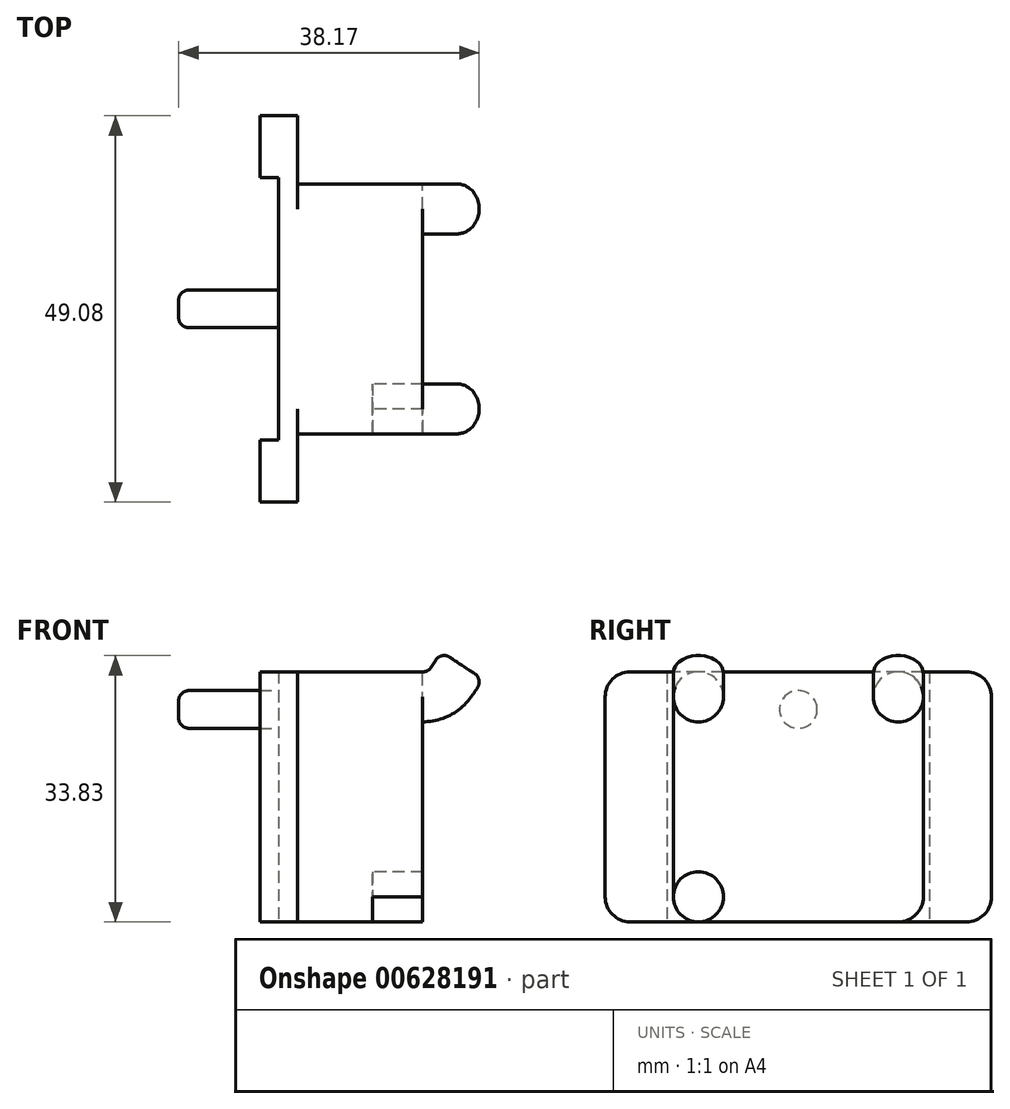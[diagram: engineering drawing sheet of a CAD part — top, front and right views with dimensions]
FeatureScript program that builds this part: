
annotation { "Feature Type Name" : "Feature", "Feature Type Description" : "" }
export const myFeature = defineFeature(function(context is Context, id is Id, definition is map)
    precondition{}
    {
        {
            var Q0;
            Q0=qCreatedBy(makeId("Right.planeOp"),FACE);
            var sketch = newSketch(context, id + "F0", { "sketchPlane" : qUnion([Q0])});
            skLineSegment(sketch, "E0.bottom", {"start": v(15.88, -15.87) * mm, "end": v(-15.88, -15.88) * mm});
            skLineSegment(sketch, "E0.top", {"start": v(15.88, 15.88) * mm, "end": v(-15.88, 15.88) * mm});
            skLineSegment(sketch, "E0.left", {"start": v(15.88, -15.87) * mm, "end": v(15.88, 15.88) * mm});
            skLineSegment(sketch, "E0.right", {"start": v(-15.88, -15.88) * mm, "end": v(-15.88, 15.88) * mm});
            skPoint(sketch, "E0.middle", {"position": v(0, 0) * mm});
            skSolve(sketch);
        }
        {
            var Q0;
            Q0=makeQuery(id+"F0.imprint","IMPRINT",FACE,{"disambiguationData":[TD([[makeQuery(id+"F0.imprint","IMPRINT",EDGE,{"derivedFrom":sQuery(id+"F0.wireOp",EDGE,"E0.bottom")}),-1.0]])]});
            extrude(context, id + "F1", {"entities" : qUnion([Q0]), "depth" : 9.52 * mm, "offsetDistance" : 25.4 * mm});
        }
        {
            var Q0;
            Q0=makeQuery(id+"F1.opExtrude","CAP_FACE",FACE,{"disambiguationData":[OSD([sQuery(id+"F0.wireOp",EDGE,"E0.bottom"),sQuery(id+"F0.wireOp",EDGE,"E0.top"),sQuery(id+"F0.wireOp",EDGE,"E0.left"),sQuery(id+"F0.wireOp",EDGE,"E0.right")])],"isStart":false});
            var sketch = newSketch(context, id + "F2", { "sketchPlane" : qUnion([Q0])});
            skCircle(sketch, "E1", {"center": v(-12.7, 12.7) * mm, "radius": 3.18 * mm});
            skLineSegment(sketch, "E2", {"start": v(-24.57, 0) * mm, "end": v(19.39, 0) * mm, "construction": true});
            skPoint(sketch, "E2.endSnap0", {"position": v(-15.88, 0) * mm});
            skLineSegment(sketch, "E3", {"start": v(0, 20.38) * mm, "end": v(0, -18.88) * mm, "construction": true});
            skCircle(sketch, "E4.MirrorC", {"center": v(-12.7, -12.7) * mm, "radius": 3.18 * mm});
            skLineSegment(sketch, "E5.MirrorCS", {"start": v(0, -20.38) * mm, "end": v(0, 18.88) * mm, "construction": true});
            skCircle(sketch, "E6.MirrorC", {"center": v(12.7, 12.7) * mm, "radius": 3.18 * mm});
            skCircle(sketch, "E7.MirrorC", {"center": v(12.7, -12.7) * mm, "radius": 3.18 * mm});
            skLineSegment(sketch, "E8", {"start": v(-12.7, 15.88) * mm, "end": v(-12.7, -15.88) * mm, "construction": true});
            skLineSegment(sketch, "E9", {"start": v(-15.88, 12.7) * mm, "end": v(15.88, 12.7) * mm, "construction": true});
            skPoint(sketch, "E10", {"position": v(-12.7, 15.88) * mm});
            skPoint(sketch, "E11", {"position": v(0, 0) * mm});
            skSolve(sketch);
        }
        {
            var Q0;
            Q0=makeQuery(id+"F1.opExtrude","SWEPT_FACE",FACE,{"disambiguationData":[OSD([sQuery(id+"F0.wireOp",EDGE,"E0.top")])]});
            var sketch = newSketch(context, id + "F3", { "sketchPlane" : qUnion([Q0])});
            skLineSegment(sketch, "E12", {"start": v(0, -12.7) * mm, "end": v(9.53, -12.7) * mm, "construction": true});
            skSolve(sketch);
        }
        {
            var Q0;
            Q0=sQuery(id+"F3.wireOp",VERTEX,"E12.start");
            var Q1;
            Q1=sQuery(id+"F2.wireOp",VERTEX,"E10");
            var Q2;
            Q2=sQuery(id+"F2.wireOp",VERTEX,"E8.end");
            cPlane(context, id + "F4", {"entities" : qUnion([Q0, Q1, Q2]), "cplaneType" : CPlaneType.THREE_POINT, "offset" : 25.4 * mm, "width" : 152.4 * mm, "height" : 152.4 * mm});
        }
        {
            var Q0;
            Q0=qCreatedBy(id+"F4.planeOp",FACE);
            var sketch = newSketch(context, id + "F5", { "sketchPlane" : qUnion([Q0])});
            skLineSegment(sketch, "E13", {"start": v(9.53, 9.53) * mm, "end": v(9.53, 15.88) * mm});
            skLineSegment(sketch, "E14", {"start": v(9.53, 9.53) * mm, "end": v(15.88, 9.53) * mm});
            skArc(sketch, "E15", {"start": v(15.88, 9.53) * mm, "mid": v(19.48, 10.43) * mm, "end": v(22.23, 12.93) * mm});
            skLineSegment(sketch, "E16", {"start": v(22.23, 12.93) * mm, "end": v(23.55, 14.93) * mm});
            skSolve(sketch);
        }
        {
            var Q0;
            {var subQ0=sQuery(id+"F2.wireOp",EDGE,"E1");var subQ1=makeQuery(id+"F2.imprint","INTERSECT",VERTEX,{"derivedFrom":[makeQuery(id+"F1.opExtrude","CAP_EDGE",EDGE,{"disambiguationData":[OSD([sQuery(id+"F0.wireOp",EDGE,"E0.top")])],"isStart":false}),subQ0]});Q0=makeQuery(id+"F2.imprint","IMPRINT",FACE,{"disambiguationData":[TD([[makeQuery(id+"F2.imprint","IMPRINT",EDGE,{"disambiguationData":[TD([[subQ1,-1.0]])],"derivedFrom":subQ0}),1.0]])]});}
            var Q1;
            Q1=qSketchRegion(id+"F5",true);
            var Q2;
            Q2=sQuery(id+"F5.wireOp",EDGE,"E14");
            var Q3;
            Q3=sQuery(id+"F5.wireOp",EDGE,"E15");
            var Q4;
            Q4=sQuery(id+"F5.wireOp",EDGE,"E16");
            sweep(context, id + "F6", {"operationType" : NewBodyOperationType.ADD, "profiles" : qUnion([Q0, Q1]), "path" : qUnion([Q2, Q3, Q4])});
        }
        {
            var Q0;
            Q0=makeQuery(id+"F6.opSweep","CAP_FACE",FACE,{"disambiguationData":[OSD([sQuery(id+"F2.wireOp",EDGE,"E1"),sQuery(id+"F5.wireOp",VERTEX,"E16.end")])],"isStart":false});
            fillet(context, id + "F7", {"entities" : qUnion([Q0]), "radius" : 1.27 * mm, "tangentPropagation" : true, "allowEdgeOverflow" : false});
        }
        {
            var Q0;
            {var subQ0=sQuery(id+"F0.wireOp",EDGE,"E0.top");Q0=makeQuery(id+"F3.imprint","IMPRINT",FACE,{"disambiguationData":[TD([[makeQuery(id+"F3.imprint","IMPRINT",EDGE,{"derivedFrom":makeQuery(id+"F1.opExtrude","CAP_EDGE",EDGE,{"disambiguationData":[OSD([subQ0])],"isStart":true})}),1.0]])]});}
            var sketch = newSketch(context, id + "F8", { "sketchPlane" : qUnion([Q0])});
            skLineSegment(sketch, "E17", {"start": v(12.55, 0) * mm, "end": v(0, 0) * mm, "construction": true});
            skSolve(sketch);
        }
        {
            var Q0;
            Q0=sQuery(id+"F8.wireOp",VERTEX,"E17.end");
            var Q1;
            Q1=sQuery(id+"F8.wireOp",VERTEX,"E17.start");
            var Q2;
            Q2=sQuery(id+"F2.wireOp",VERTEX,"E11");
            cPlane(context, id + "F9", {"entities" : qUnion([Q0, Q1, Q2]), "cplaneType" : CPlaneType.THREE_POINT, "offset" : 25.4 * mm, "width" : 152.4 * mm, "height" : 152.4 * mm});
        }
        {
            var Q0;
            Q0=makeQuery(id+"F1.opExtrude","SWEPT_BODY",BODY,{"disambiguationData":[OSD([sQuery(id+"F0.wireOp",EDGE,"E0.bottom"),sQuery(id+"F0.wireOp",EDGE,"E0.top"),sQuery(id+"F0.wireOp",EDGE,"E0.left"),sQuery(id+"F0.wireOp",EDGE,"E0.right")])]});
            var Q1;
            Q1=qCreatedBy(id+"F9.planeOp",FACE);
            mirror(context, id + "F10", {"operationType" : NewBodyOperationType.ADD, "entities" : qUnion([Q0]), "mirrorPlane" : qUnion([Q1])});
        }
        {
            var Q0;
            {var subQ0=sQuery(id+"F2.wireOp",EDGE,"E4.MirrorC");var subQ1=makeQuery(id+"F2.imprint","INTERSECT",VERTEX,{"derivedFrom":[makeQuery(id+"F1.opExtrude","CAP_EDGE",EDGE,{"disambiguationData":[OSD([sQuery(id+"F0.wireOp",EDGE,"E0.bottom")])],"isStart":false}),subQ0]});Q0=makeQuery(id+"F2.imprint","IMPRINT",FACE,{"disambiguationData":[TD([[makeQuery(id+"F2.imprint","IMPRINT",EDGE,{"disambiguationData":[TD([[subQ1,-1.0]])],"derivedFrom":subQ0}),-1.0]])]});}
            var Q1;
            {var subQ0=sQuery(id+"F2.wireOp",EDGE,"E7.MirrorC");var subQ1=makeQuery(id+"F2.imprint","INTERSECT",VERTEX,{"derivedFrom":[makeQuery(id+"F1.opExtrude","CAP_EDGE",EDGE,{"disambiguationData":[OSD([sQuery(id+"F0.wireOp",EDGE,"E0.bottom")])],"isStart":false}),subQ0]});Q1=makeQuery(id+"F2.imprint","IMPRINT",FACE,{"disambiguationData":[TD([[makeQuery(id+"F2.imprint","IMPRINT",EDGE,{"disambiguationData":[TD([[subQ1,-1.0]])],"derivedFrom":subQ0}),1.0]])]});}
            extrude(context, id + "F11", {"entities" : qUnion([Q0, Q1]), "operationType" : NewBodyOperationType.ADD, "depth" : 6.35 * mm, "offsetDistance" : 25.4 * mm});
        }
        {
            var Q0;
            Q0=makeQuery(id+"F1.opExtrude","SWEPT_EDGE",EDGE,{"disambiguationData":[OSD([sQuery(id+"F0.wireOp",EDGE,"E0.top"),sQuery(id+"F0.wireOp",EDGE,"E0.right")])]});
            var Q1;
            Q1=makeQuery(id+"F1.opExtrude","SWEPT_EDGE",EDGE,{"disambiguationData":[OSD([sQuery(id+"F0.wireOp",EDGE,"E0.bottom"),sQuery(id+"F0.wireOp",EDGE,"E0.right")])]});
            var Q2;
            Q2=makeQuery(id+"F1.opExtrude","SWEPT_EDGE",EDGE,{"disambiguationData":[OSD([sQuery(id+"F0.wireOp",EDGE,"E0.bottom"),sQuery(id+"F0.wireOp",EDGE,"E0.left")])]});
            var Q3;
            Q3=makeQuery(id+"F1.opExtrude","SWEPT_EDGE",EDGE,{"disambiguationData":[OSD([sQuery(id+"F0.wireOp",EDGE,"E0.top"),sQuery(id+"F0.wireOp",EDGE,"E0.left")])]});
            fillet(context, id + "F12", {"entities" : qUnion([Q0, Q1, Q2, Q3]), "radius" : 3.17 * mm, "tangentPropagation" : true, "allowEdgeOverflow" : false});
        }
        {
            var Q0;
            Q0=makeQuery(id+"F1.opExtrude","CAP_FACE",FACE,{"disambiguationData":[OSD([sQuery(id+"F0.wireOp",EDGE,"E0.bottom"),sQuery(id+"F0.wireOp",EDGE,"E0.top"),sQuery(id+"F0.wireOp",EDGE,"E0.left"),sQuery(id+"F0.wireOp",EDGE,"E0.right")])],"isStart":true});
            var sketch = newSketch(context, id + "F13", { "sketchPlane" : qUnion([Q0])});
            skLineSegment(sketch, "E18.bottom", {"start": v(-24.54, 15.88) * mm, "end": v(24.54, 15.88) * mm});
            skLineSegment(sketch, "E18.top", {"start": v(-24.54, -15.88) * mm, "end": v(24.54, -15.88) * mm});
            skLineSegment(sketch, "E18.left", {"start": v(-24.54, 15.87) * mm, "end": v(-24.54, -15.87) * mm});
            skLineSegment(sketch, "E18.right", {"start": v(24.54, 15.87) * mm, "end": v(24.54, -15.87) * mm});
            skPoint(sketch, "E18.middle", {"position": v(0, 0) * mm});
            skSolve(sketch);
        }
        {
            var Q0;
            Q0=makeQuery(id+"F13.imprint","IMPRINT",FACE,{"disambiguationData":[TD([[makeQuery(id+"F13.imprint","IMPRINT",EDGE,{"derivedFrom":sQuery(id+"F13.wireOp",EDGE,"E18.bottom")}),-1.0]])]});
            var Q1;
            {var subQ1=sQuery(id+"F0.wireOp",EDGE,"E0.left");Q1=makeQuery(id+"F13.imprint","IMPRINT",FACE,{"disambiguationData":[TD([[makeQuery(id+"F13.imprint","IMPRINT",EDGE,{"derivedFrom":makeQuery(id+"F1.opExtrude","CAP_EDGE",EDGE,{"disambiguationData":[OSD([subQ1])],"isStart":true})}),-1.0]])]});}
            extrude(context, id + "F14", {"entities" : qUnion([Q0, Q1]), "operationType" : NewBodyOperationType.ADD, "depth" : 4.8 * mm, "offsetDistance" : 25.4 * mm});
        }
        {
            var Q0;
            Q0=makeQuery(id+"F14.opExtrude","CAP_FACE",FACE,{"disambiguationData":[OSD([sQuery(id+"F13.wireOp",EDGE,"E18.bottom"),sQuery(id+"F13.wireOp",EDGE,"E18.top"),sQuery(id+"F13.wireOp",EDGE,"E18.left"),sQuery(id+"F13.wireOp",EDGE,"E18.right")])],"isStart":false});
            var sketch = newSketch(context, id + "F15", { "sketchPlane" : qUnion([Q0])});
            skLineSegment(sketch, "E19.bottom", {"start": v(-16.66, 15.88) * mm, "end": v(16.66, 15.88) * mm});
            skLineSegment(sketch, "E19.top", {"start": v(-16.66, -15.88) * mm, "end": v(16.66, -15.88) * mm});
            skLineSegment(sketch, "E19.left", {"start": v(-16.66, 15.88) * mm, "end": v(-16.66, -15.88) * mm});
            skLineSegment(sketch, "E19.right", {"start": v(16.66, 15.87) * mm, "end": v(16.66, -15.88) * mm});
            skPoint(sketch, "E19.middle", {"position": v(0, 0) * mm});
            skSolve(sketch);
        }
        {
            var Q0;
            Q0=makeQuery(id+"F15.imprint","IMPRINT",FACE,{"disambiguationData":[TD([[makeQuery(id+"F15.imprint","IMPRINT",EDGE,{"derivedFrom":sQuery(id+"F15.wireOp",EDGE,"E19.bottom")}),-1.0]])]});
            extrude(context, id + "F16", {"entities" : qUnion([Q0]), "operationType" : NewBodyOperationType.REMOVE, "oppositeDirection" : true, "depth" : 2.4 * mm, "offsetDistance" : 25.4 * mm});
        }
        {
            var Q0;
            Q0=makeQuery(id+"F16.boolean.opBoolean","COPY",FACE,{"derivedFrom":makeQuery(id+"F16.opExtrude","CAP_FACE",FACE,{"disambiguationData":[OSD([sQuery(id+"F15.wireOp",EDGE,"E19.bottom"),sQuery(id+"F15.wireOp",EDGE,"E19.top"),sQuery(id+"F15.wireOp",EDGE,"E19.left"),sQuery(id+"F15.wireOp",EDGE,"E19.right")])],"isStart":false})});
            var sketch = newSketch(context, id + "F17", { "sketchPlane" : qUnion([Q0])});
            skCircle(sketch, "E20", {"center": v(0, 11.1) * mm, "radius": 2.39 * mm});
            skSolve(sketch);
        }
        {
            var Q0;
            Q0=makeQuery(id+"F17.imprint","IMPRINT",FACE,{"disambiguationData":[TD([[makeQuery(id+"F17.imprint","IMPRINT",EDGE,{"derivedFrom":sQuery(id+"F17.wireOp",EDGE,"E20")}),1.0]])]});
            extrude(context, id + "F18", {"entities" : qUnion([Q0]), "operationType" : NewBodyOperationType.ADD, "depth" : 12.7 * mm, "offsetDistance" : 25.4 * mm});
        }
        {
            var Q0;
            Q0=makeQuery(id+"F14.opExtrude","SWEPT_EDGE",EDGE,{"disambiguationData":[OSD([sQuery(id+"F13.wireOp",EDGE,"E18.bottom"),sQuery(id+"F13.wireOp",EDGE,"E18.left")])]});
            var Q1;
            Q1=makeQuery(id+"F14.opExtrude","SWEPT_EDGE",EDGE,{"disambiguationData":[OSD([sQuery(id+"F13.wireOp",EDGE,"E18.top"),sQuery(id+"F13.wireOp",EDGE,"E18.left")])]});
            var Q2;
            Q2=makeQuery(id+"F14.opExtrude","SWEPT_EDGE",EDGE,{"disambiguationData":[OSD([sQuery(id+"F13.wireOp",EDGE,"E18.top"),sQuery(id+"F13.wireOp",EDGE,"E18.right")])]});
            var Q3;
            Q3=makeQuery(id+"F14.opExtrude","SWEPT_EDGE",EDGE,{"disambiguationData":[OSD([sQuery(id+"F13.wireOp",EDGE,"E18.bottom"),sQuery(id+"F13.wireOp",EDGE,"E18.right")])]});
            fillet(context, id + "F19", {"entities" : qUnion([Q0, Q1, Q2, Q3]), "radius" : 3.17 * mm, "tangentPropagation" : true, "allowEdgeOverflow" : false});
        }
        {
            var Q0;
            Q0=makeQuery(id+"F18.opExtrude","CAP_FACE",FACE,{"disambiguationData":[OSD([sQuery(id+"F17.wireOp",EDGE,"E20")])],"isStart":false});
            fillet(context, id + "F20", {"entities" : qUnion([Q0]), "radius" : 1.27 * mm, "tangentPropagation" : true, "allowEdgeOverflow" : false});
        }
    });
